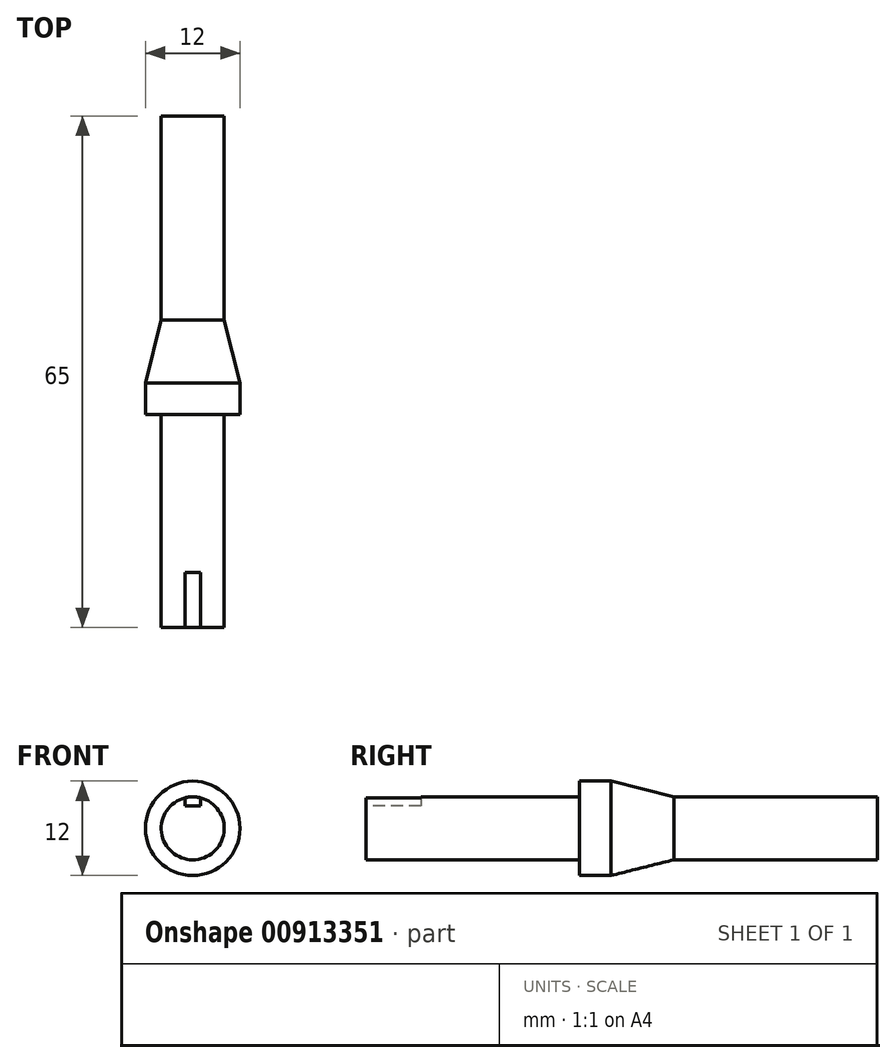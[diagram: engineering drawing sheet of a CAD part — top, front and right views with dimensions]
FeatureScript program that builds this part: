
annotation { "Feature Type Name" : "Feature", "Feature Type Description" : "" }
export const myFeature = defineFeature(function(context is Context, id is Id, definition is map)
    precondition{}
    {
        {
            var Q0;
            Q0=qCreatedBy(makeId("Front.planeOp"),FACE);
            var sketch = newSketch(context, id + "F0", { "sketchPlane" : qUnion([Q0])});
            skCircle(sketch, "E0", {"center": v(0, 0) * mm, "radius": 4 * mm});
            skSolve(sketch);
        }
        {
            var Q0;
            Q0 = qSketchRegion(id + "F0", true);
            extrude(context, id + "F1", {"entities" : qUnion([Q0]), "depth" : 65 * mm, "offsetDistance" : 25 * mm});
        }
        {
            var Q0;
            Q0=makeQuery(id+"F1.opExtrude","CAP_FACE",FACE,{"disambiguationData":[OSD([sQuery(id+"F0.wireOp",EDGE,"E0")])],"isStart":false});
            cPlane(context, id + "F2", {"entities" : qUnion([Q0]), "cplaneType" : CPlaneType.OFFSET, "offset" : 27.1 * mm, "oppositeDirection" : true, "width" : 150 * mm, "height" : 150 * mm});
        }
        {
            var Q0;
            Q0=qCreatedBy(id+"F2.planeOp",FACE);
            var sketch = newSketch(context, id + "F3", { "sketchPlane" : qUnion([Q0])});
            skCircle(sketch, "E1", {"center": v(0, 0) * mm, "radius": 6 * mm});
            skSolve(sketch);
        }
        {
            var Q0;
            Q0 = qSketchRegion(id + "F3", true);
            extrude(context, id + "F4", {"entities" : qUnion([Q0]), "operationType" : NewBodyOperationType.ADD, "oppositeDirection" : true, "depth" : 4 * mm, "offsetDistance" : 25 * mm});
        }
        {
            var Q0;
            Q0=makeQuery(id+"F4.boolean.opBoolean","INTERSECT",EDGE,{"derivedFrom":[makeQuery(id+"F1.opExtrude","SWEPT_FACE",FACE,{"disambiguationData":[OSD([sQuery(id+"F0.wireOp",EDGE,"E0")])]}),makeQuery(id+"F4.opExtrude","CAP_FACE",FACE,{"disambiguationData":[OSD([sQuery(id+"F3.wireOp",EDGE,"E1")])],"isStart":false})]});
            chamfer(context, id + "F5", {"entities" : qUnion([Q0]), "chamferType" : ChamferType.TWO_OFFSETS, "width1" : 2 * mm, "oppositeDirection" : false, "width2" : 8 * mm, "tangentPropagation" : true});
        }
        {
            var Q0;
            Q0=makeQuery(id+"F1.opExtrude","CAP_FACE",FACE,{"disambiguationData":[OSD([sQuery(id+"F0.wireOp",EDGE,"E0")])],"isStart":false});
            var sketch = newSketch(context, id + "F6", { "sketchPlane" : qUnion([Q0])});
            skCircle(sketch, "E2.0", {"center": v(0, 0) * mm, "radius": 4 * mm, "construction": true});
            skLineSegment(sketch, "E3", {"start": v(-1, 3.87) * mm, "end": v(-1, 2.87) * mm});
            skLineSegment(sketch, "E4", {"start": v(-1, 2.87) * mm, "end": v(1, 2.87) * mm});
            skLineSegment(sketch, "E5", {"start": v(1, 2.87) * mm, "end": v(1, 3.87) * mm});
            skLineSegment(sketch, "E6", {"start": v(1, 3.87) * mm, "end": v(0, 4.41) * mm});
            skLineSegment(sketch, "E7", {"start": v(0, 4.41) * mm, "end": v(-1, 3.87) * mm});
            skSolve(sketch);
        }
        {
            var Q0;
            Q0 = qSketchRegion(id + "F6", true);
            extrude(context, id + "F7", {"entities" : qUnion([Q0]), "operationType" : NewBodyOperationType.REMOVE, "oppositeDirection" : true, "depth" : 7 * mm, "offsetDistance" : 25 * mm});
        }
        {
            var Q0;
            Q0=qCreatedBy(makeId("Front.planeOp"),FACE);
            cPlane(context, id + "F8", {"entities" : qUnion([Q0]), "cplaneType" : CPlaneType.OFFSET, "offset" : (65 / 2) * mm, "width" : 150 * mm, "height" : 150 * mm});
        }
    });
